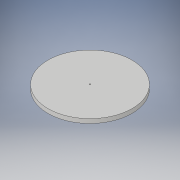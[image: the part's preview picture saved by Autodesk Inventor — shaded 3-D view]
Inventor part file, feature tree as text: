
AUTODESK INVENTOR PART (.ipt)
format: ipt  version: 2017 (Build 210142000, 142)  size: 107,520 bytes
history: native  units: mm
features: sketch x3, extrude x2, hole x1
ambient origin geometry x8: Origin, YZ Plane, XZ Plane, XY Plane, X Axis, Y Axis, Z Axis, Center Point
bodies: Solid1 (feature_tree)
feature tree (6):
  extrude  "Extrusion1"  Depth=3.0mm
  extrude  "Extrusion2"  Depth=20.0mm
  hole  "Hole1"  [1 undecoded]
  sketch  "Sketch1"  dims[d0=60.0mm d1=3.0mm]
  sketch  "Sketch2"  dims[d2=0.0mm d3=20.0mm]
  sketch  "Sketch3"  dims[d4=4.0mm d5=0.0mm d6=1.0mm d7=6.0mm d8=4.0mm d9=2.0mm d10=90.0deg d11=8.0mm d12=20.594885mm]
note: 1 required parameter value undecoded (feature->parameter linkage not recoverable at this tier; creation-order binding heuristic only, values carry confidence <= 0.55)
